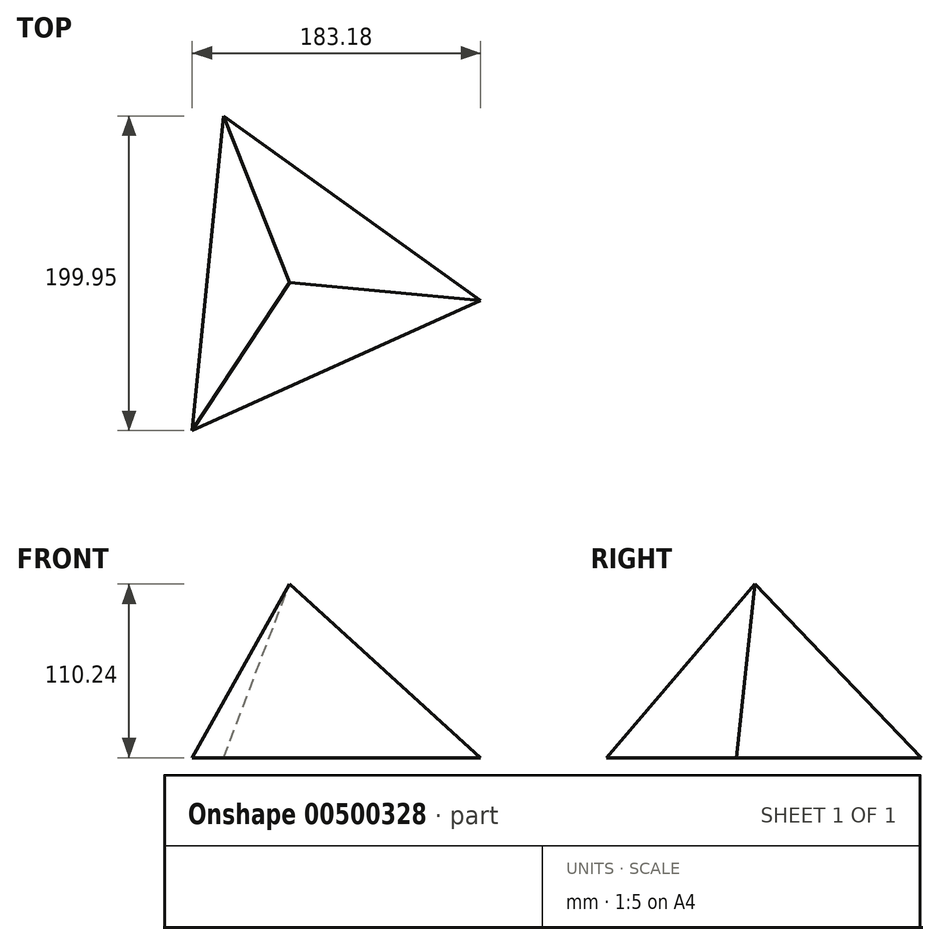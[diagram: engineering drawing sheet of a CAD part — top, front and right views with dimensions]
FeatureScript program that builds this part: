
annotation { "Feature Type Name" : "Feature", "Feature Type Description" : "" }
export const myFeature = defineFeature(function(context is Context, id is Id, definition is map)
    precondition{}
    {
        {
            var Q0;
            Q0=qCreatedBy(makeId("Top.planeOp"),FACE);
            var sketch = newSketch(context, id + "F0", { "sketchPlane" : qUnion([Q0])});
            skCircle(sketch, "E0.cCircle", {"center": v(0, 0) * mm, "radius": 116.02 * mm, "construction": true});
            skLineSegment(sketch, "E0.0", {"start": v(-47.7, 105.76) * mm, "end": v(115.44, -11.57) * mm});
            skLineSegment(sketch, "E0.1", {"start": v(115.44, -11.57) * mm, "end": v(-67.74, -94.19) * mm});
            skLineSegment(sketch, "E0.2", {"start": v(-67.74, -94.19) * mm, "end": v(-47.7, 105.76) * mm});
            skSolve(sketch);
        }
        {
            var Q0;
            Q0=qCreatedBy(makeId("Top.planeOp"),FACE);
            cPlane(context, id + "F1", {"entities" : qUnion([Q0]), "cplaneType" : CPlaneType.OFFSET, "offset" : 110.24 * mm, "width" : 152.4 * mm, "height" : 152.4 * mm});
        }
        {
            var Q0;
            Q0=qCreatedBy(id+"F1.planeOp",FACE);
            var sketch = newSketch(context, id + "F2", { "sketchPlane" : qUnion([Q0])});
            skPoint(sketch, "E1", {"position": v(-5.87, 0) * mm});
            skSolve(sketch);
        }
        {
            var Q0;
            Q0=makeQuery(id+"F0.imprint","IMPRINT",FACE,{"disambiguationData":[TD([[makeQuery(id+"F0.imprint","IMPRINT",EDGE,{"derivedFrom":sQuery(id+"F0.wireOp",EDGE,"E0.0")}),-1.0]])]});
            var Q1;
            Q1=sQuery(id+"F2.wireOp",VERTEX,"E1");
            loft(context, id + "F3", {"sheetProfilesArray" : [{ "sheetProfileEntities" : qUnion([Q0]) }, { "sheetProfileEntities" : qUnion([Q1]) }]});
        }
    });
